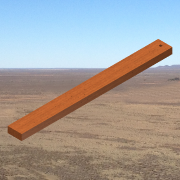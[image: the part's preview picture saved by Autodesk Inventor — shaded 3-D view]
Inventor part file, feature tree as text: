
AUTODESK INVENTOR PART (.ipt)
format: ipt  version: 2014 SP1 (Build 180222100, 222)  size: 136,704 bytes
history: native  units: in
note: dims shown in document units (in); Inventor stores cm internally (conversion verified against a paired STEP export)
features: sketch x2, extrude x1, hole x1
ambient origin geometry x8: Origin, YZ Plane, XZ Plane, XY Plane, X Axis, Y Axis, Z Axis, Center Point
bodies: Solid1 (feature_tree)
feature tree (4):
  extrude  "Extrusion1"  Depth=0.65in
  hole  "Hole2"  [1 undecoded]
  sketch  "Sketch1"  dims[d0=1.5in d1=0.65in]
  sketch  "Sketch3"  dims[d2=16.0in d3=0.0in d11=0.25in d12=0.25in d13=0.75in d14=0.375in d15=0.25in d16=0.5635in d17=1.0in d18=0.8108in d19=0.5in]
note: 1 required parameter value undecoded (feature->parameter linkage not recoverable at this tier; creation-order binding heuristic only, values carry confidence <= 0.55)
